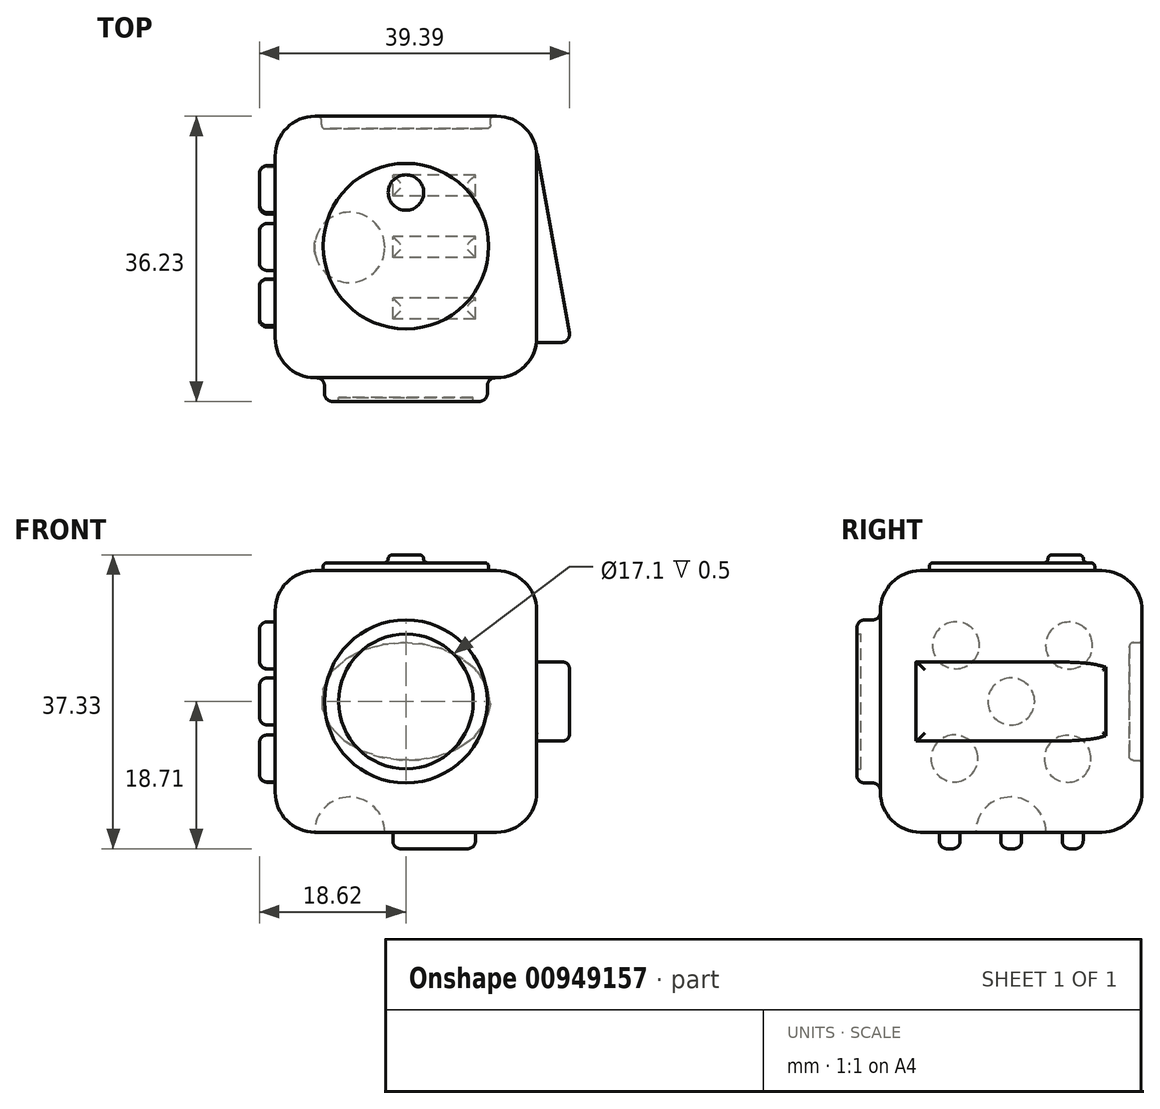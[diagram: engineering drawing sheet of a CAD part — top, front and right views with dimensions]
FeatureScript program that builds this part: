
annotation { "Feature Type Name" : "Feature", "Feature Type Description" : "" }
export const myFeature = defineFeature(function(context is Context, id is Id, definition is map)
    precondition{}
    {
        {
            var Q0;
            Q0=qCreatedBy(makeId("Front.planeOp"),FACE);
            var sketch = newSketch(context, id + "F0", { "sketchPlane" : qUnion([Q0])});
            skLineSegment(sketch, "E0.bottom", {"start": v(-16.61, 16.61) * mm, "end": v(16.61, 16.61) * mm});
            skLineSegment(sketch, "E0.top", {"start": v(-16.61, -16.61) * mm, "end": v(16.61, -16.61) * mm});
            skLineSegment(sketch, "E0.left", {"start": v(-16.61, 16.61) * mm, "end": v(-16.61, -16.61) * mm});
            skLineSegment(sketch, "E0.right", {"start": v(16.61, 16.62) * mm, "end": v(16.61, -16.61) * mm});
            skSolve(sketch);
        }
        {
            var Q0;
            Q0=makeQuery(id+"F0.imprint","IMPRINT",FACE,{"disambiguationData":[TD([[makeQuery(id+"F0.imprint","IMPRINT",EDGE,{"derivedFrom":sQuery(id+"F0.wireOp",EDGE,"E0.bottom")}),-1.0]])]});
            extrude(context, id + "F1", {"entities" : qUnion([Q0]), "depth" : 33.23 * mm, "offsetDistance" : 25.4 * mm});
        }
        {
            var Q0;
            Q0=makeQuery(id+"F1.opExtrude","CAP_FACE",FACE,{"disambiguationData":[OSD([sQuery(id+"F0.wireOp",EDGE,"E0.bottom"),sQuery(id+"F0.wireOp",EDGE,"E0.top"),sQuery(id+"F0.wireOp",EDGE,"E0.left"),sQuery(id+"F0.wireOp",EDGE,"E0.right")])],"isStart":false});
            var sketch = newSketch(context, id + "F2", { "sketchPlane" : qUnion([Q0])});
            skCircle(sketch, "E1", {"center": v(0, 0) * mm, "radius": 10.35 * mm});
            skCircle(sketch, "E2", {"center": v(0, 0) * mm, "radius": 8.55 * mm});
            skSolve(sketch);
        }
        {
            var Q0;
            Q0=makeQuery(id+"F2.imprint","IMPRINT",FACE,{"disambiguationData":[TD([[makeQuery(id+"F2.imprint","IMPRINT",EDGE,{"derivedFrom":sQuery(id+"F2.wireOp",EDGE,"E1")}),1.0]])]});
            extrude(context, id + "F3", {"entities" : qUnion([Q0]), "operationType" : NewBodyOperationType.ADD, "depth" : 3 * mm, "offsetDistance" : 25.4 * mm});
        }
        {
            var Q0;
            Q0=makeQuery(id+"F3.boolean.opBoolean","SPLIT",FACE,{"disambiguationData":[TD([makeQuery(id+"F3.opExtrude","SWEPT_FACE",FACE,{"disambiguationData":[OSD([sQuery(id+"F2.wireOp",EDGE,"E2")])]})])],"derivedFrom":makeQuery(id+"F1.opExtrude","CAP_FACE",FACE,{"disambiguationData":[OSD([sQuery(id+"F0.wireOp",EDGE,"E0.bottom"),sQuery(id+"F0.wireOp",EDGE,"E0.top"),sQuery(id+"F0.wireOp",EDGE,"E0.left"),sQuery(id+"F0.wireOp",EDGE,"E0.right")])],"isStart":false})});
            extrude(context, id + "F4", {"entities" : qUnion([Q0]), "operationType" : NewBodyOperationType.ADD, "depth" : 2.5 * mm, "offsetDistance" : 25.4 * mm});
        }
        {
            var Q0;
            Q0=makeQuery(id+"F1.opExtrude","SWEPT_FACE",FACE,{"disambiguationData":[OSD([sQuery(id+"F0.wireOp",EDGE,"E0.right")])]});
            var Q1;
            Q1=makeQuery(id+"F1.opExtrude","SWEPT_FACE",FACE,{"disambiguationData":[OSD([sQuery(id+"F0.wireOp",EDGE,"E0.left")])]});
            var Q2;
            Q2=makeQuery(id+"F1.opExtrude","SWEPT_FACE",FACE,{"disambiguationData":[OSD([sQuery(id+"F0.wireOp",EDGE,"E0.bottom")])]});
            var Q3;
            Q3=makeQuery(id+"F1.opExtrude","CAP_FACE",FACE,{"disambiguationData":[OSD([sQuery(id+"F0.wireOp",EDGE,"E0.bottom"),sQuery(id+"F0.wireOp",EDGE,"E0.top"),sQuery(id+"F0.wireOp",EDGE,"E0.left"),sQuery(id+"F0.wireOp",EDGE,"E0.right")])],"isStart":true});
            var Q4;
            Q4=makeQuery(id+"F1.opExtrude","SWEPT_FACE",FACE,{"disambiguationData":[OSD([sQuery(id+"F0.wireOp",EDGE,"E0.top")])]});
            fillet(context, id + "F5", {"entities" : qUnion([Q0, Q1, Q2, Q3, Q4]), "radius" : 5.08 * mm, "tangentPropagation" : true, "allowEdgeOverflow" : false});
        }
        {
            var Q0;
            Q0=makeQuery(id+"F3.opExtrude","SWEPT_FACE",FACE,{"disambiguationData":[OSD([sQuery(id+"F2.wireOp",EDGE,"E1")])]});
            fillet(context, id + "F6", {"entities" : qUnion([Q0]), "radius" : 1 * mm, "tangentPropagation" : true, "allowEdgeOverflow" : false});
        }
        {
            var Q0;
            Q0=makeQuery(id+"F1.opExtrude","SWEPT_FACE",FACE,{"disambiguationData":[OSD([sQuery(id+"F0.wireOp",EDGE,"E0.right")])]});
            var sketch = newSketch(context, id + "F7", { "sketchPlane" : qUnion([Q0])});
            skLineSegment(sketch, "E3.bottom", {"start": v(-28.87, 4.85) * mm, "end": v(-4.37, 4.85) * mm});
            skLineSegment(sketch, "E3.top", {"start": v(-28.87, -5.15) * mm, "end": v(-4.37, -5.15) * mm});
            skLineSegment(sketch, "E3.left", {"start": v(-28.87, 4.85) * mm, "end": v(-28.87, -5.15) * mm});
            skLineSegment(sketch, "E3.right", {"start": v(-4.37, 4.85) * mm, "end": v(-4.37, -5.15) * mm});
            skSolve(sketch);
        }
        {
            var Q0;
            Q0=qCreatedBy(makeId("Top.planeOp"),FACE);
            var sketch = newSketch(context, id + "F8", { "sketchPlane" : qUnion([Q0])});
            skLineSegment(sketch, "E4", {"start": v(16.6, -4.23) * mm, "end": v(16.6, -28.73) * mm});
            skLineSegment(sketch, "E5", {"start": v(16.6, -4.23) * mm, "end": v(20.96, -28.73) * mm});
            skLineSegment(sketch, "E6", {"start": v(20.96, -28.73) * mm, "end": v(16.6, -28.73) * mm});
            skSolve(sketch);
        }
        {
            var Q0;
            Q0=makeQuery(id+"F8.imprint","IMPRINT",FACE,{"disambiguationData":[TD([[makeQuery(id+"F8.imprint","IMPRINT",EDGE,{"derivedFrom":sQuery(id+"F8.wireOp",EDGE,"E4")}),1.0]])]});
            extrude(context, id + "F9", {"entities" : qUnion([Q0]), "operationType" : NewBodyOperationType.ADD, "depth" : 5 * mm, "offsetDistance" : 25.4 * mm});
        }
        {
            var Q0;
            Q0=makeQuery(id+"F9.opExtrude","CAP_FACE",FACE,{"disambiguationData":[OSD([sQuery(id+"F8.wireOp",EDGE,"E4"),sQuery(id+"F8.wireOp",EDGE,"E5"),sQuery(id+"F8.wireOp",EDGE,"E6")])],"isStart":true});
            extrude(context, id + "F10", {"entities" : qUnion([Q0]), "operationType" : NewBodyOperationType.ADD, "depth" : 5 * mm, "offsetDistance" : 25.4 * mm});
        }
        {
            var Q0;
            Q0=makeQuery(id+"F1.opExtrude","SWEPT_FACE",FACE,{"disambiguationData":[OSD([sQuery(id+"F0.wireOp",EDGE,"E0.top")])]});
            var sketch = newSketch(context, id + "F11", { "sketchPlane" : qUnion([Q0])});
            skLineSegment(sketch, "E7.bottom", {"start": v(8.83, 25.75) * mm, "end": v(-1.67, 25.75) * mm});
            skLineSegment(sketch, "E7.top", {"start": v(8.83, 23.1) * mm, "end": v(-1.67, 23.1) * mm});
            skLineSegment(sketch, "E7.left", {"start": v(8.83, 25.75) * mm, "end": v(8.83, 23.1) * mm});
            skLineSegment(sketch, "E7.right", {"start": v(-1.67, 25.75) * mm, "end": v(-1.67, 23.1) * mm});
            skLineSegment(sketch, "E8.bottom", {"start": v(8.83, 17.94) * mm, "end": v(-1.67, 17.94) * mm});
            skLineSegment(sketch, "E8.top", {"start": v(8.83, 15.28) * mm, "end": v(-1.67, 15.28) * mm});
            skLineSegment(sketch, "E8.left", {"start": v(8.83, 17.94) * mm, "end": v(8.83, 15.28) * mm});
            skLineSegment(sketch, "E8.right", {"start": v(-1.67, 17.94) * mm, "end": v(-1.67, 15.28) * mm});
            skLineSegment(sketch, "E9.bottom", {"start": v(8.83, 10.13) * mm, "end": v(-1.67, 10.13) * mm});
            skLineSegment(sketch, "E9.top", {"start": v(8.83, 7.47) * mm, "end": v(-1.67, 7.47) * mm});
            skLineSegment(sketch, "E9.left", {"start": v(8.83, 10.13) * mm, "end": v(8.83, 7.47) * mm});
            skLineSegment(sketch, "E9.right", {"start": v(-1.67, 10.13) * mm, "end": v(-1.67, 7.47) * mm});
            skLineSegment(sketch, "E10", {"start": v(-2.68, 16.66) * mm, "end": v(-11.61, 16.66) * mm});
            skArc(sketch, "E11", {"start": v(-11.61, 16.66) * mm, "mid": v(-7.15, 12.2) * mm, "end": v(-2.68, 16.67) * mm});
            skArc(sketch, "E12", {"start": v(-2.68, 16.67) * mm, "mid": v(-7.15, 21.13) * mm, "end": v(-11.61, 16.66) * mm});
            skSolve(sketch);
        }
        {
            var Q0;
            {var subQ0=sQuery(id+"F8.wireOp",EDGE,"E5");Q0=makeQuery(id+"F10.boolean.opBoolean","MERGE",FACE,{"derivedFrom":[makeQuery(id+"F9.opExtrude","SWEPT_FACE",FACE,{"disambiguationData":[OSD([subQ0])]}),makeQuery(id+"F10.opExtrude","SWEPT_FACE",FACE,{"disambiguationData":[OSD([subQ0])]})]});}
            fillet(context, id + "F12", {"entities" : qUnion([Q0]), "radius" : 1 * mm, "tangentPropagation" : true, "allowEdgeOverflow" : false});
        }
        {
            var Q0;
            {var subQ0=sQuery(id+"F11.wireOp",EDGE,"E12");var subQ1=sQuery(id+"F11.wireOp",EDGE,"E10");var subQ2=makeQuery(id+"F11.imprint","INTERSECT",VERTEX,{"disambiguationData":[OD(0.0)],"derivedFrom":[subQ1,sQuery(id+"F11.wireOp",EDGE,"E11"),subQ0]});Q0=makeQuery(id+"F11.imprint","IMPRINT",FACE,{"disambiguationData":[TD([[makeQuery(id+"F11.imprint","IMPRINT",EDGE,{"disambiguationData":[TD([[subQ2,-1.0]])],"derivedFrom":subQ1}),-1.0]])]});}
            var Q1;
            {var subQ0=sQuery(id+"F11.wireOp",EDGE,"E12");var subQ1=sQuery(id+"F11.wireOp",EDGE,"E10");var subQ2=makeQuery(id+"F11.imprint","INTERSECT",VERTEX,{"disambiguationData":[OD(1.0)],"derivedFrom":[subQ1,sQuery(id+"F11.wireOp",EDGE,"E11"),subQ0]});Q1=makeQuery(id+"F11.imprint","IMPRINT",FACE,{"disambiguationData":[TD([[makeQuery(id+"F11.imprint","IMPRINT",EDGE,{"disambiguationData":[TD([[subQ2,1.0]])],"derivedFrom":subQ1}),-1.0]])]});}
            var Q2;
            Q2=sQuery(id+"F11.wireOp",EDGE,"E10");
            revolve(context, id + "F13", {"operationType" : NewBodyOperationType.ADD, "surfaceOperationType" : NewSurfaceOperationType.NEW, "entities" : qUnion([Q0, Q1]), "axis" : qUnion([Q2]), "revolveType" : RevolveType.SYMMETRIC, "angle" : 360 * degree});
        }
        {
            var Q0;
            Q0=makeQuery(id+"F1.opExtrude","CAP_FACE",FACE,{"disambiguationData":[OSD([sQuery(id+"F0.wireOp",EDGE,"E0.bottom"),sQuery(id+"F0.wireOp",EDGE,"E0.top"),sQuery(id+"F0.wireOp",EDGE,"E0.left"),sQuery(id+"F0.wireOp",EDGE,"E0.right")])],"isStart":true});
            var sketch = newSketch(context, id + "F14", { "sketchPlane" : qUnion([Q0])});
            skEllipse(sketch, "E13", {"center": v(0, 0) * mm, "majorRadius": 7.47 * mm, "minorRadius": 10.74 * mm, "majorAxis": v(-0.03, 1)});
            skLineSegment(sketch, "E14", {"start": v(-10.74, -0.05) * mm, "end": v(10.73, -0.05) * mm});
            skSolve(sketch);
        }
        {
            var Q0;
            {var subQ0=sQuery(id+"F14.wireOp",EDGE,"E14");Q0=makeQuery(id+"F14.imprint","IMPRINT",FACE,{"disambiguationData":[TD([[makeQuery(id+"F14.imprint","IMPRINT",EDGE,{"derivedFrom":subQ0}),1.0]])]});}
            var Q1;
            {var subQ0=sQuery(id+"F14.wireOp",EDGE,"E14");Q1=makeQuery(id+"F14.imprint","IMPRINT",FACE,{"disambiguationData":[TD([[makeQuery(id+"F14.imprint","IMPRINT",EDGE,{"derivedFrom":subQ0}),-1.0]])]});}
            extrude(context, id + "F15", {"entities" : qUnion([Q0, Q1]), "operationType" : NewBodyOperationType.REMOVE, "oppositeDirection" : true, "depth" : 1.6 * mm, "offsetDistance" : 25.4 * mm});
        }
        {
            var Q0;
            Q0=makeQuery(id+"F15.boolean.opBoolean","COPY",FACE,{"derivedFrom":makeQuery(id+"F15.opExtrude","SWEPT_FACE",FACE,{"disambiguationData":[OSD([sQuery(id+"F14.wireOp",EDGE,"E13")])]})});
            fillet(context, id + "F16", {"entities" : qUnion([Q0]), "radius" : .5 * mm, "tangentPropagation" : true, "allowEdgeOverflow" : false});
        }
        {
            var Q0;
            Q0=makeQuery(id+"F1.opExtrude","SWEPT_FACE",FACE,{"disambiguationData":[OSD([sQuery(id+"F0.wireOp",EDGE,"E0.left")])]});
            var sketch = newSketch(context, id + "F17", { "sketchPlane" : qUnion([Q0])});
            skCircle(sketch, "E15", {"center": v(16.61, 0) * mm, "radius": 2.98 * mm});
            skCircle(sketch, "E16", {"center": v(9.44, -7.28) * mm, "radius": 2.98 * mm});
            skCircle(sketch, "E17", {"center": v(23.82, -7.24) * mm, "radius": 2.98 * mm});
            skCircle(sketch, "E18", {"center": v(9.26, 7.1) * mm, "radius": 2.98 * mm});
            skCircle(sketch, "E19", {"center": v(23.64, 7.13) * mm, "radius": 2.98 * mm});
            skSolve(sketch);
        }
        {
            var Q0;
            Q0=makeQuery(id+"F1.opExtrude","SWEPT_FACE",FACE,{"disambiguationData":[OSD([sQuery(id+"F0.wireOp",EDGE,"E0.bottom")])]});
            var sketch = newSketch(context, id + "F18", { "sketchPlane" : qUnion([Q0])});
            skCircle(sketch, "E20", {"center": v(0, -16.52) * mm, "radius": 10.52 * mm});
            skCircle(sketch, "E21", {"center": v(0, -9.7) * mm, "radius": 2.25 * mm});
            skSolve(sketch);
        }
        {
            var Q0;
            Q0=makeQuery(id+"F18.imprint","IMPRINT",FACE,{"disambiguationData":[TD([[makeQuery(id+"F18.imprint","IMPRINT",EDGE,{"derivedFrom":sQuery(id+"F18.wireOp",EDGE,"E20")}),1.0]])]});
            extrude(context, id + "F19", {"entities" : qUnion([Q0]), "operationType" : NewBodyOperationType.ADD, "depth" : 1 * mm, "offsetDistance" : 25.4 * mm});
        }
        {
            var Q0;
            Q0=makeQuery(id+"F19.boolean.opBoolean","SPLIT",FACE,{"disambiguationData":[TD([makeQuery(id+"F19.opExtrude","SWEPT_FACE",FACE,{"disambiguationData":[OSD([sQuery(id+"F18.wireOp",EDGE,"E21")])]})])],"derivedFrom":makeQuery(id+"F1.opExtrude","SWEPT_FACE",FACE,{"disambiguationData":[OSD([sQuery(id+"F0.wireOp",EDGE,"E0.bottom")])]})});
            extrude(context, id + "F20", {"entities" : qUnion([Q0]), "operationType" : NewBodyOperationType.ADD, "depth" : 2 * mm, "offsetDistance" : 25.4 * mm});
        }
        {
            var Q0;
            Q0=makeQuery(id+"F19.opExtrude","CAP_FACE",FACE,{"disambiguationData":[OSD([sQuery(id+"F18.wireOp",EDGE,"E20"),sQuery(id+"F18.wireOp",EDGE,"E21")])],"isStart":false});
            fillet(context, id + "F21", {"entities" : qUnion([Q0]), "radius" : .5 * mm, "tangentPropagation" : true, "allowEdgeOverflow" : false});
        }
        {
            var Q0;
            Q0=makeQuery(id+"F20.opExtrude","CAP_FACE",FACE,{"disambiguationData":[OSD([sQuery(id+"F0.wireOp",EDGE,"E0.bottom")])],"isStart":false});
            fillet(context, id + "F22", {"entities" : qUnion([Q0]), "radius" : .5 * mm, "tangentPropagation" : true, "allowEdgeOverflow" : false});
        }
        {
            var Q0;
            Q0=makeQuery(id+"F17.imprint","IMPRINT",FACE,{"disambiguationData":[TD([[makeQuery(id+"F17.imprint","IMPRINT",EDGE,{"derivedFrom":sQuery(id+"F17.wireOp",EDGE,"E18")}),1.0]])]});
            var Q1;
            Q1=makeQuery(id+"F17.imprint","IMPRINT",FACE,{"disambiguationData":[TD([[makeQuery(id+"F17.imprint","IMPRINT",EDGE,{"derivedFrom":sQuery(id+"F17.wireOp",EDGE,"E15")}),1.0]])]});
            var Q2;
            Q2=makeQuery(id+"F17.imprint","IMPRINT",FACE,{"disambiguationData":[TD([[makeQuery(id+"F17.imprint","IMPRINT",EDGE,{"derivedFrom":sQuery(id+"F17.wireOp",EDGE,"E19")}),1.0]])]});
            var Q3;
            Q3=makeQuery(id+"F17.imprint","IMPRINT",FACE,{"disambiguationData":[TD([[makeQuery(id+"F17.imprint","IMPRINT",EDGE,{"derivedFrom":sQuery(id+"F17.wireOp",EDGE,"E17")}),1.0]])]});
            var Q4;
            Q4=makeQuery(id+"F17.imprint","IMPRINT",FACE,{"disambiguationData":[TD([[makeQuery(id+"F17.imprint","IMPRINT",EDGE,{"derivedFrom":sQuery(id+"F17.wireOp",EDGE,"E16")}),1.0]])]});
            extrude(context, id + "F23", {"entities" : qUnion([Q0, Q1, Q2, Q3, Q4]), "operationType" : NewBodyOperationType.ADD, "depth" : 2 * mm, "offsetDistance" : 25.4 * mm});
        }
        {
            var Q0;
            Q0=makeQuery(id+"F23.opExtrude","CAP_FACE",FACE,{"disambiguationData":[OSD([sQuery(id+"F17.wireOp",EDGE,"E18")])],"isStart":false});
            var Q1;
            Q1=makeQuery(id+"F23.opExtrude","CAP_FACE",FACE,{"disambiguationData":[OSD([sQuery(id+"F17.wireOp",EDGE,"E15")])],"isStart":false});
            var Q2;
            Q2=makeQuery(id+"F23.opExtrude","CAP_FACE",FACE,{"disambiguationData":[OSD([sQuery(id+"F17.wireOp",EDGE,"E16")])],"isStart":false});
            var Q3;
            Q3=makeQuery(id+"F23.opExtrude","CAP_FACE",FACE,{"disambiguationData":[OSD([sQuery(id+"F17.wireOp",EDGE,"E17")])],"isStart":false});
            var Q4;
            Q4=makeQuery(id+"F23.opExtrude","CAP_FACE",FACE,{"disambiguationData":[OSD([sQuery(id+"F17.wireOp",EDGE,"E19")])],"isStart":false});
            fillet(context, id + "F24", {"entities" : qUnion([Q0, Q1, Q2, Q3, Q4]), "radius" : 1 * mm, "tangentPropagation" : true, "allowEdgeOverflow" : false});
        }
        {
            var Q0;
            Q0=makeQuery(id+"F11.imprint","IMPRINT",FACE,{"disambiguationData":[TD([[makeQuery(id+"F11.imprint","IMPRINT",EDGE,{"derivedFrom":sQuery(id+"F11.wireOp",EDGE,"E7.bottom")}),1.0]])]});
            var Q1;
            Q1=makeQuery(id+"F11.imprint","IMPRINT",FACE,{"disambiguationData":[TD([[makeQuery(id+"F11.imprint","IMPRINT",EDGE,{"derivedFrom":sQuery(id+"F11.wireOp",EDGE,"E8.bottom")}),1.0]])]});
            var Q2;
            Q2=makeQuery(id+"F11.imprint","IMPRINT",FACE,{"disambiguationData":[TD([[makeQuery(id+"F11.imprint","IMPRINT",EDGE,{"derivedFrom":sQuery(id+"F11.wireOp",EDGE,"E9.bottom")}),1.0]])]});
            extrude(context, id + "F25", {"entities" : qUnion([Q0, Q1, Q2]), "operationType" : NewBodyOperationType.ADD, "depth" : 2.1 * mm, "offsetDistance" : 25.4 * mm});
        }
        {
            var Q0;
            Q0=makeQuery(id+"F25.opExtrude","CAP_FACE",FACE,{"disambiguationData":[OSD([sQuery(id+"F11.wireOp",EDGE,"E7.bottom"),sQuery(id+"F11.wireOp",EDGE,"E7.top"),sQuery(id+"F11.wireOp",EDGE,"E7.left"),sQuery(id+"F11.wireOp",EDGE,"E7.right")])],"isStart":false});
            var Q1;
            Q1=makeQuery(id+"F25.opExtrude","CAP_FACE",FACE,{"disambiguationData":[OSD([sQuery(id+"F11.wireOp",EDGE,"E8.bottom"),sQuery(id+"F11.wireOp",EDGE,"E8.top"),sQuery(id+"F11.wireOp",EDGE,"E8.left"),sQuery(id+"F11.wireOp",EDGE,"E8.right")])],"isStart":false});
            var Q2;
            Q2=makeQuery(id+"F25.opExtrude","CAP_FACE",FACE,{"disambiguationData":[OSD([sQuery(id+"F11.wireOp",EDGE,"E9.bottom"),sQuery(id+"F11.wireOp",EDGE,"E9.top"),sQuery(id+"F11.wireOp",EDGE,"E9.left"),sQuery(id+"F11.wireOp",EDGE,"E9.right")])],"isStart":false});
            fillet(context, id + "F26", {"entities" : qUnion([Q0, Q1, Q2]), "radius" : 1 * mm, "tangentPropagation" : true, "allowEdgeOverflow" : false});
        }
    });
